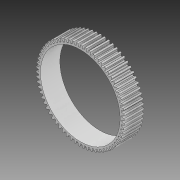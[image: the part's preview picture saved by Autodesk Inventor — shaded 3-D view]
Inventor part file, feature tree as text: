
AUTODESK INVENTOR PART (.ipt)
format: ipt  version: 2020 (Build 240168000, 168)  size: 1,056,256 bytes
history: native  units: mm
features: extrude x2, sketch x2, fillet x1, pattern_circular x1
ambient origin geometry x8: Origin, YZ Plane, XZ Plane, XY Plane, X Axis, Y Axis, Z Axis, Center Point
bodies: Solid1 (feature_tree)
feature tree (6):
  extrude  "Extrusion1"  Depth=1.3mm
  extrude  "Extrusion3"  Depth=10.0mm TaperAngle=0.0deg
  fillet  "Fillet2"  Radius=660.0mm
  pattern_circular  "Circular Pattern2"  [2 undecoded]
  sketch  "Sketch1"  dims[d0=64.1mm d1=1.3mm]
  sketch  "Sketch3"  dims[d2=15.0mm d3=0.0mm d12=0.8mm d13=1.8mm d14=8.726646mm d15=0.523599mm d16=0.523599mm d17=0.523599mm d18=0.523599mm d19=0.523599mm d20=2.792527mm d21=0.523599mm d22=64.1mm d23=66.683194mm d24=1.677942mm d25=9.19019mm d26=7.512247mm d27=5.834305mm d28=4.156362mm d29=2.47842mm d30=0.523599mm d31=0.523599mm d32=0.523599mm d33=0.523599mm d34=0.523599mm d35=10.868132mm d36=12.546074mm d37=14.224017mm d38=15.901959mm d39=17.579902mm d40=0.523599mm d41=0.523599mm d42=19.257844mm d43=20.935786mm d44=0.224037mm d45=68.620589mm d46=10.0mm d47=0.0mm d48=660.0mm d49=360.0deg d51=0.65mm]
note: 2 required parameter values undecoded (feature->parameter linkage not recoverable at this tier; creation-order binding heuristic only, values carry confidence <= 0.55)
